# Revit family: Electrical_Controls_Conspec_Fireray-One-Smoke-Detector
name_source: partatom
category: Electrical Fixtures
units: mm (PartAtom-declared; Revit-internal decimal feet)

## family parameters
Classification Number = 23.85.30.21
Cut with Voids When Loaded = No
Host = Face
Maintain Annotation Orientation = No
Part Type = Normal
Room Calculation Point = No
Round Connector Dimension = Use Diameter
Shared = No

## types (1)
- Fireray One Smoke Detector
    Apparent Load = 0 VA
    Assembly Code = D5030
    Beam Path Clearance = 3.3ft in diameter from center line between Detector and Reflector
    Current Consumption All Operational Modes = 5 mA
    Current Consumption Fast Alignment Mode = 33 mA
    Date Updated = 2023/10/17
    Default Elevation = 0 "
    Depth = 5.28 "
    Description = Standalone Fireray One beam smoke detector that prioritizes ease of installation.
    Detector Location = Within the ceiling jet flow (top 10% of the floor to ceiling height) unless otherwise stipulated
    Dynamic Beam Phasing = Allows beam detectors to be mounted facing each other with the reflectors in the middle. liminates false alarms caused by crosstalk between beams
    Height = 7.13 "
    Housing = UL94 V0 Polycarbonate, IP55, UV stable, white
    Keynote = 16000
    Lateral Spacing Between Detectors = 60ft maximum as per NFPA 72
    Manufacturer = CONSPEC Controls
    Max. Angular Alignment = ±4.5° (±70° with adjustment bracket accessory)
    Model = Fireray One Smoke Detector
    Multi-detector Arrangement = Dynamic Beam Phasing allows for Detectors to face each other with the reflectors in the middle
    Number of Poles = 3
    Operating Humidity = 0% to 93% RH Non-Condesing
    Operating Temperature = -4°F to +131°F
    Power Factor = 0.8
    Product Material = Conspec - Plastic - PC - White
    Product data url = https://bimobject.com
    Signal Output = Individual Alarm and Fault relays (VFCO) 0.5A @ 30 VDC
    URL = https://www.conspec-controls.com
    Version = 1
    Voltage = 36 V
    Voltage Range = 14V - 36V DC
    Weight = 1.55 lbf
    Width = 5.12 "

## geometry (parser evidence)
native form markers: Sweep x2
no freeform markers — native parametric forms only
